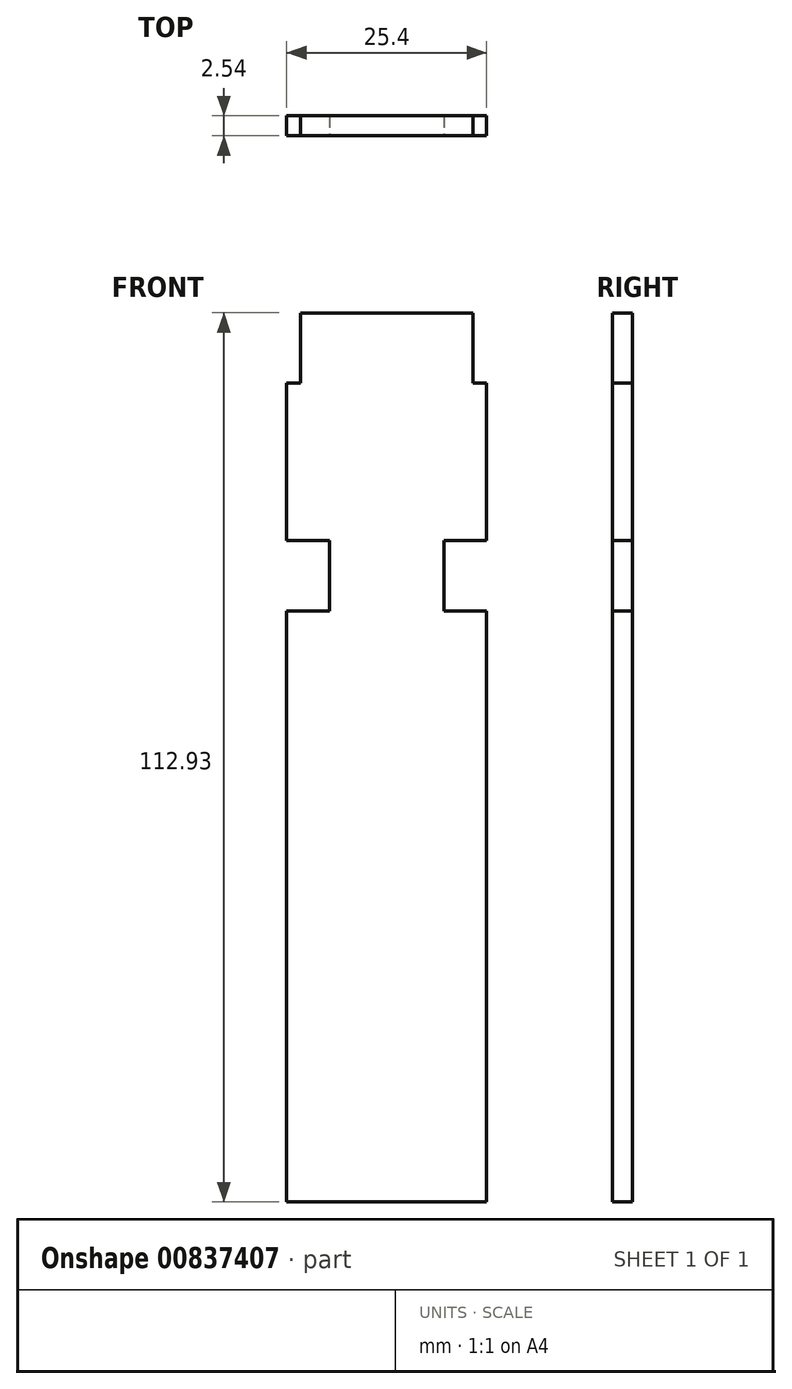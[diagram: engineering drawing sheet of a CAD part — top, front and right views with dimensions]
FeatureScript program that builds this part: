
annotation { "Feature Type Name" : "Feature", "Feature Type Description" : "" }
export const myFeature = defineFeature(function(context is Context, id is Id, definition is map)
    precondition{}
    {
        {
            var Q0;
            Q0=qCreatedBy(makeId("Front.planeOp"),FACE);
            var sketch = newSketch(context, id + "F0", { "sketchPlane" : qUnion([Q0])});
            skLineSegment(sketch, "E0", {"start": v(0, 0) * mm, "end": v(-12.7, 0) * mm});
            skLineSegment(sketch, "E1.MirrorCS", {"start": v(0, 0) * mm, "end": v(12.7, 0) * mm});
            skLineSegment(sketch, "E2", {"start": v(-12.7, 0) * mm, "end": v(-12.7, 75.03) * mm});
            skLineSegment(sketch, "E3", {"start": v(-12.7, 75.03) * mm, "end": v(12.7, 75.03) * mm});
            skLineSegment(sketch, "E4", {"start": v(12.7, 75.03) * mm, "end": v(12.7, 0) * mm});
            skLineSegment(sketch, "E5", {"start": v(-7.28, 75.03) * mm, "end": v(-7.28, 84) * mm});
            skLineSegment(sketch, "E6", {"start": v(7.28, 75.03) * mm, "end": v(7.28, 84) * mm});
            skLineSegment(sketch, "E7", {"start": v(-7.28, 84) * mm, "end": v(7.28, 84) * mm});
            skLineSegment(sketch, "E8", {"start": v(0, 84) * mm, "end": v(-12.7, 84) * mm});
            skPoint(sketch, "E8.startSnap0", {"position": v(0, 75.03) * mm});
            skLineSegment(sketch, "E9.MirrorCS", {"start": v(0, 84) * mm, "end": v(12.7, 84) * mm});
            skLineSegment(sketch, "E10", {"start": v(-12.7, 84) * mm, "end": v(-12.7, 104.01) * mm});
            skLineSegment(sketch, "E11", {"start": v(-12.7, 104.01) * mm, "end": v(12.7, 104.01) * mm});
            skLineSegment(sketch, "E12", {"start": v(12.7, 104.01) * mm, "end": v(12.7, 84) * mm});
            skLineSegment(sketch, "E13", {"start": v(-10.92, 104.01) * mm, "end": v(-10.92, 112.93) * mm});
            skLineSegment(sketch, "E14", {"start": v(10.92, 104.01) * mm, "end": v(10.92, 112.93) * mm});
            skLineSegment(sketch, "E15", {"start": v(10.92, 112.93) * mm, "end": v(-10.92, 112.93) * mm});
            skSolve(sketch);
        }
        {
            var Q0;
            Q0=makeQuery(id+"F0.imprint","IMPRINT",FACE,{"disambiguationData":[TD([[makeQuery(id+"F0.imprint","IMPRINT",EDGE,{"derivedFrom":sQuery(id+"F0.wireOp",EDGE,"E0")}),-1.0]])]});
            var Q1;
            {var subQ1=sQuery(id+"F0.wireOp",EDGE,"E5");Q1=makeQuery(id+"F0.imprint","IMPRINT",FACE,{"disambiguationData":[TD([[makeQuery(id+"F0.imprint","IMPRINT",EDGE,{"derivedFrom":subQ1}),-1.0]])]});}
            var Q2;
            {var subQ6=sQuery(id+"F0.wireOp",EDGE,"E10");Q2=makeQuery(id+"F0.imprint","IMPRINT",FACE,{"disambiguationData":[TD([[makeQuery(id+"F0.imprint","IMPRINT",EDGE,{"derivedFrom":subQ6}),-1.0]])]});}
            var Q3;
            {var subQ0=sQuery(id+"F0.wireOp",EDGE,"E13");Q3=makeQuery(id+"F0.imprint","IMPRINT",FACE,{"disambiguationData":[TD([[makeQuery(id+"F0.imprint","IMPRINT",EDGE,{"derivedFrom":subQ0}),-1.0]])]});}
            extrude(context, id + "F1", {"entities" : qUnion([Q0, Q1, Q2, Q3]), "oppositeDirection" : true, "depth" : 2.54 * mm, "offsetDistance" : 25.4 * mm});
        }
    });
